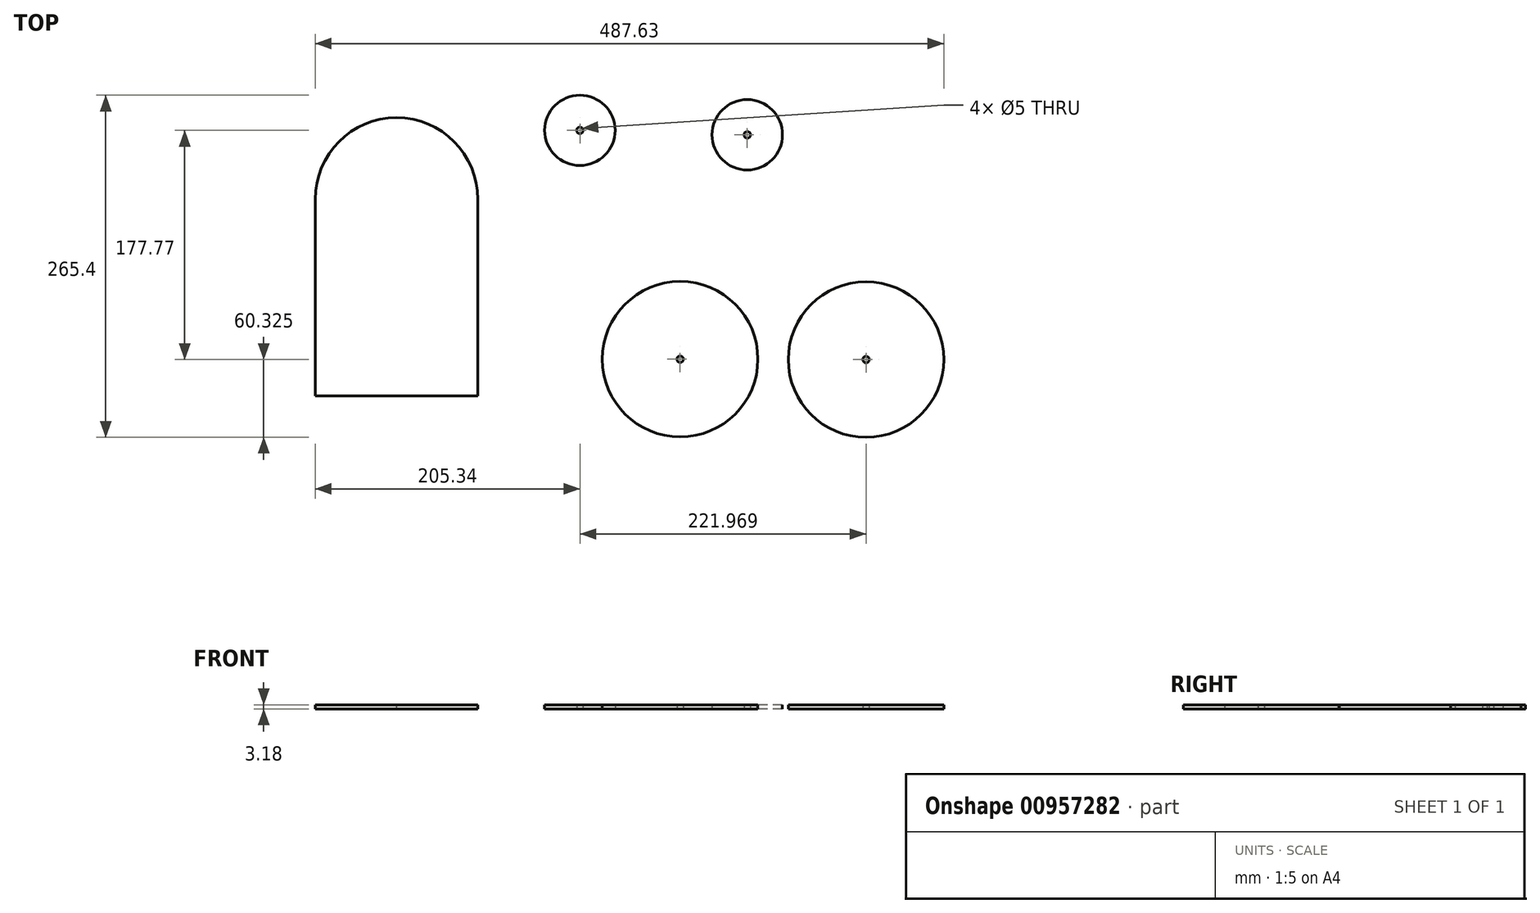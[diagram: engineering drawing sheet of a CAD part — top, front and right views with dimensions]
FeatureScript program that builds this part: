
annotation { "Feature Type Name" : "Feature", "Feature Type Description" : "" }
export const myFeature = defineFeature(function(context is Context, id is Id, definition is map)
    precondition{}
    {
        {
            var Q0;
            Q0=qCreatedBy(makeId("Top.planeOp"),FACE);
            var sketch = newSketch(context, id + "F0", { "sketchPlane" : qUnion([Q0])});
            skLineSegment(sketch, "E0", {"start": v(147.98, -136.97) * mm, "end": v(147.98, -289.37) * mm});
            skLineSegment(sketch, "E1", {"start": v(274.15, -136.97) * mm, "end": v(274.15, -289.37) * mm});
            skLineSegment(sketch, "E2", {"start": v(274.15, -289.37) * mm, "end": v(147.98, -289.37) * mm});
            skArc(sketch, "E3.filletArc", {"start": v(211.48, -73.47) * mm, "mid": v(166.58, -92.07) * mm, "end": v(147.98, -136.97) * mm});
            skArc(sketch, "E4.filletArc", {"start": v(274.15, -136.97) * mm, "mid": v(255.55, -92.07) * mm, "end": v(210.65, -73.47) * mm});
            skLineSegment(sketch, "E5", {"start": v(211.36, -73.47) * mm, "end": v(211.36, -136.97) * mm});
            skLineSegment(sketch, "E6", {"start": v(211.36, -136.97) * mm, "end": v(208.05, -136.97) * mm});
            skLineSegment(sketch, "E7", {"start": v(208, -73.47) * mm, "end": v(208, -136.97) * mm});
            skCircle(sketch, "E8", {"center": v(353.32, -83.45) * mm, "radius": 27.3 * mm});
            skCircle(sketch, "E9", {"center": v(431.1, -260.97) * mm, "radius": 60.33 * mm});
            skCircle(sketch, "E10", {"center": v(575.29, -261.22) * mm, "radius": 60.33 * mm});
            skCircle(sketch, "E11", {"center": v(483.16, -86.9) * mm, "radius": 27.3 * mm});
            skCircle(sketch, "E12", {"center": v(353.32, -83.45) * mm, "radius": 2.5 * mm});
            skCircle(sketch, "E13", {"center": v(483.16, -86.9) * mm, "radius": 2.5 * mm});
            skCircle(sketch, "E14", {"center": v(431.1, -260.97) * mm, "radius": 2.5 * mm});
            skCircle(sketch, "E15", {"center": v(575.29, -261.22) * mm, "radius": 2.5 * mm});
            skSolve(sketch);
        }
        {
            var Q0;
            Q0=makeQuery(id+"F0.imprint","IMPRINT",FACE,{"disambiguationData":[TD([[makeQuery(id+"F0.imprint","IMPRINT",EDGE,{"derivedFrom":sQuery(id+"F0.wireOp",EDGE,"E9")}),1.0]])]});
            var Q1;
            Q1=makeQuery(id+"F0.imprint","IMPRINT",FACE,{"disambiguationData":[TD([[makeQuery(id+"F0.imprint","IMPRINT",EDGE,{"derivedFrom":sQuery(id+"F0.wireOp",EDGE,"E10")}),1.0]])]});
            var Q2;
            Q2=makeQuery(id+"F0.imprint","IMPRINT",FACE,{"disambiguationData":[TD([[makeQuery(id+"F0.imprint","IMPRINT",EDGE,{"derivedFrom":sQuery(id+"F0.wireOp",EDGE,"E11")}),1.0]])]});
            var Q3;
            {var subQ1=sQuery(id+"F0.wireOp",EDGE,"E0");Q3=makeQuery(id+"F0.imprint","IMPRINT",FACE,{"disambiguationData":[TD([[makeQuery(id+"F0.imprint","IMPRINT",EDGE,{"derivedFrom":subQ1}),1.0]])]});}
            var Q4;
            Q4=makeQuery(id+"F0.imprint","IMPRINT",FACE,{"disambiguationData":[TD([[makeQuery(id+"F0.imprint","IMPRINT",EDGE,{"derivedFrom":sQuery(id+"F0.wireOp",EDGE,"E8")}),1.0]])]});
            extrude(context, id + "F1", {"entities" : qUnion([Q0, Q1, Q2, Q3, Q4]), "depth" : 3.17 * mm, "offsetDistance" : 25.4 * mm});
        }
    });
